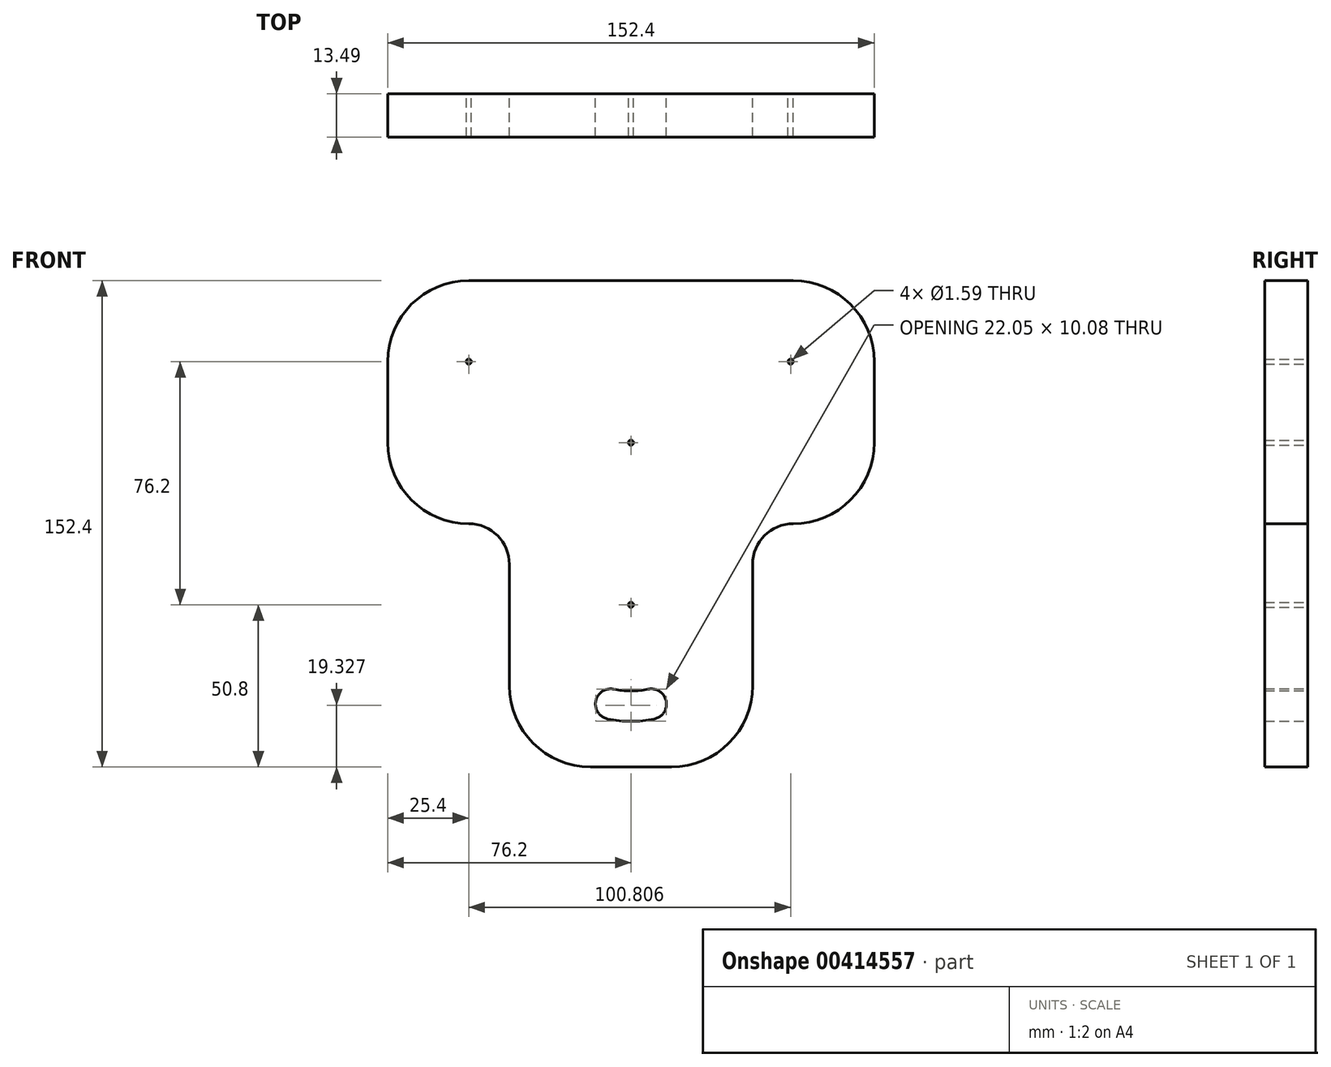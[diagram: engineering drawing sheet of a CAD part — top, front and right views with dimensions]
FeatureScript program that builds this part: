
annotation { "Feature Type Name" : "Feature", "Feature Type Description" : "" }
export const myFeature = defineFeature(function(context is Context, id is Id, definition is map)
    precondition{}
    {
        {
            var Q0;
            Q0=qCreatedBy(makeId("Front.planeOp"),FACE);
            var sketch = newSketch(context, id + "F0", { "sketchPlane" : qUnion([Q0])});
            skLineSegment(sketch, "E0", {"start": v(-50.8, 0) * mm, "end": v(50.8, 0) * mm});
            skLineSegment(sketch, "E1", {"start": v(76.2, -25.4) * mm, "end": v(76.2, -50.8) * mm});
            skLineSegment(sketch, "E2", {"start": v(50.8, -76.2) * mm, "end": v(50.8, -76.2) * mm});
            skLineSegment(sketch, "E3", {"start": v(38.1, -88.9) * mm, "end": v(38.1, -127) * mm});
            skLineSegment(sketch, "E4", {"start": v(12.7, -152.4) * mm, "end": v(-12.7, -152.4) * mm});
            skLineSegment(sketch, "E5", {"start": v(-38.1, -127) * mm, "end": v(-38.1, -88.9) * mm});
            skLineSegment(sketch, "E6", {"start": v(-50.8, -76.2) * mm, "end": v(-50.8, -76.2) * mm});
            skLineSegment(sketch, "E7", {"start": v(-76.2, -50.8) * mm, "end": v(-76.2, -25.4) * mm});
            skLineSegment(sketch, "E8", {"start": v(0, -152.4) * mm, "end": v(0, 0) * mm, "construction": true});
            skCircle(sketch, "E9", {"center": v(0, -101.6) * mm, "radius": 0.8 * mm});
            skCircle(sketch, "E10", {"center": v(-50.8, -25.4) * mm, "radius": 0.8 * mm});
            skCircle(sketch, "E11", {"center": v(50, -25.4) * mm, "radius": 0.8 * mm});
            skCircle(sketch, "E12", {"center": v(0, -50.8) * mm, "radius": 0.8 * mm});
            skArc(sketch, "E13", {"start": v(-5.4, -128.04) * mm, "mid": v(0, -128.59) * mm, "end": v(5.4, -128.04) * mm});
            skArc(sketch, "E14", {"start": v(7.3, -137.37) * mm, "mid": v(0, -138.11) * mm, "end": v(-7.3, -137.37) * mm});
            skArc(sketch, "E15", {"start": v(7.3, -137.37) * mm, "mid": v(11.02, -131.76) * mm, "end": v(5.4, -128.04) * mm});
            skArc(sketch, "E16", {"start": v(-5.4, -128.04) * mm, "mid": v(-11.02, -131.76) * mm, "end": v(-7.3, -137.37) * mm});
            skPoint(sketch, "E17.visualSharp", {"position": v(-76.2, 0) * mm});
            skArc(sketch, "E17.filletArc", {"start": v(-50.8, 0) * mm, "mid": v(-68.76, -7.44) * mm, "end": v(-76.2, -25.4) * mm});
            skPoint(sketch, "E18.visualSharp", {"position": v(76.2, 0) * mm});
            skArc(sketch, "E18.filletArc", {"start": v(76.2, -25.4) * mm, "mid": v(68.76, -7.44) * mm, "end": v(50.8, 0) * mm});
            skPoint(sketch, "E19.visualSharp", {"position": v(-76.2, -76.2) * mm});
            skArc(sketch, "E19.filletArc", {"start": v(-76.2, -50.8) * mm, "mid": v(-68.76, -68.76) * mm, "end": v(-50.8, -76.2) * mm});
            skPoint(sketch, "E20.visualSharp", {"position": v(-38.1, -76.2) * mm});
            skArc(sketch, "E20.filletArc", {"start": v(-38.1, -88.9) * mm, "mid": v(-41.82, -79.92) * mm, "end": v(-50.8, -76.2) * mm});
            skPoint(sketch, "E21.visualSharp", {"position": v(38.1, -76.2) * mm});
            skArc(sketch, "E21.filletArc", {"start": v(50.8, -76.2) * mm, "mid": v(41.82, -79.92) * mm, "end": v(38.1, -88.9) * mm});
            skPoint(sketch, "E22.visualSharp", {"position": v(76.2, -76.2) * mm});
            skArc(sketch, "E22.filletArc", {"start": v(50.8, -76.2) * mm, "mid": v(68.76, -68.76) * mm, "end": v(76.2, -50.8) * mm});
            skPoint(sketch, "E23.visualSharp", {"position": v(-38.1, -152.4) * mm});
            skArc(sketch, "E23.filletArc", {"start": v(-38.1, -127) * mm, "mid": v(-30.66, -144.96) * mm, "end": v(-12.7, -152.4) * mm});
            skPoint(sketch, "E24.visualSharp", {"position": v(38.1, -152.4) * mm});
            skArc(sketch, "E24.filletArc", {"start": v(12.7, -152.4) * mm, "mid": v(30.66, -144.96) * mm, "end": v(38.1, -127) * mm});
            skSolve(sketch);
        }
        {
            var Q0;
            Q0=makeQuery(id+"F0.imprint","IMPRINT",FACE,{"disambiguationData":[TD([[makeQuery(id+"F0.imprint","IMPRINT",EDGE,{"derivedFrom":sQuery(id+"F0.wireOp",EDGE,"E0")}),-1.0]])]});
            extrude(context, id + "F1", {"entities" : qUnion([Q0]), "depth" : 13.5 * mm});
        }
    });
